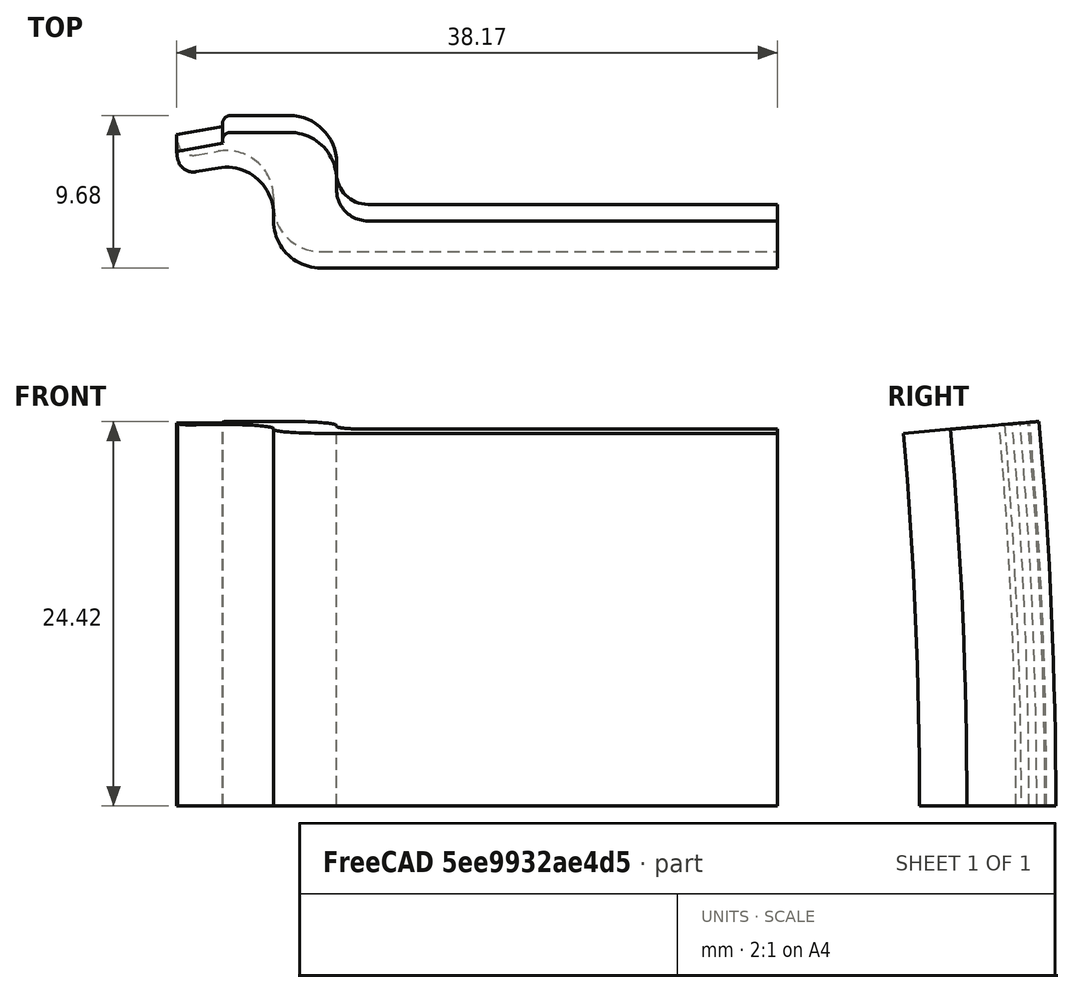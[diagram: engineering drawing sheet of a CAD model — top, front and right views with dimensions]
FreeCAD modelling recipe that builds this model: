
FCSTD DOCUMENT  (FreeCAD 0.16R)
Label: BeadLock5
License: All rights reserved
LicenseURL: http://en.wikipedia.org/wiki/All_rights_reserved
objects: PartDesign::Fillet×6, Sketcher::SketchObject×1, PartDesign::Revolution×1, Mesh::Feature×1
note: 9 computed .brp shape members not serialized (recipe doc carries the construction recipe); baked Part::Feature solids carry a one-line shape summary decoded from their .brp

FEATURE [Sketcher::SketchObject] Sketch
  sketch-geometry (10):
    g0: LineSegment StartX=0 StartY=279 StartZ=0 EndX=2.95442 EndY=279.521 EndZ=0
    g1: LineSegment StartX=2.95442 StartY=279.521 StartZ=0 EndX=2.83287 EndY=280.21 EndZ=0
    g2: LineSegment StartX=0.260472 StartY=277.523 StartZ=0 EndX=0 EndY=279 EndZ=0
    g3: LineSegment StartX=0.260472 StartY=277.523 StartZ=0 EndX=6.16932 EndY=278.565 EndZ=0
    g4: LineSegment StartX=6.16932 StartY=278.565 StartZ=0 EndX=6.16932 EndY=271.565 EndZ=0
    g5: LineSegment StartX=6.16932 StartY=271.565 StartZ=0 EndX=38.1693 EndY=271.565 EndZ=0
    g6: LineSegment StartX=38.1693 StartY=271.565 StartZ=0 EndX=38.1693 EndY=274.565 EndZ=0
    g7: LineSegment StartX=2.83287 StartY=280.21 StartZ=0 EndX=10.1693 EndY=280.21 EndZ=0
    g8: LineSegment StartX=10.1693 StartY=280.21 StartZ=0 EndX=10.1693 EndY=274.565 EndZ=0
    g9: LineSegment StartX=10.1693 StartY=274.565 StartZ=0 EndX=38.1693 EndY=274.565 EndZ=0
  constraints (30):
    c: PointOnObject(g0,g-2)
    c: DistanceY(g0) = 279
    c: Distance(g0) = 3
    c: Coincident(g1,g0)
    c: Distance(g1) = 0.7
    c: Coincident(g2,g0)
    c: Distance(g2) = 1.5
    c: Coincident(g3,g2)
    c: Distance(g3) = 6
    c: Vertical(g4)
    c: Coincident(g4,g3)
    c: Distance(g4) = 7
    c: Horizontal(g5)
    c: Coincident(g5,g4)
    c: Distance(g5) = 32
    c: Vertical(g6)
    c: Coincident(g5,g6)
    c: Distance(g6) = 3
    c: Parallel(g0,g3)
    c: Perpendicular(g0,g1)
    c: Angle(g3) = 0.174533
    c: Perpendicular(g2,g3)
    c: Coincident(g1,g7)
    c: Horizontal(g7)
    c: Coincident(g7,g8)
    c: Coincident(g8,g9)
    c: Coincident(g9,g6)
    c: Horizontal(g9)
    c: Parallel(g8,g4)
    c: Distance(g8,g4) = 4
FEATURE [PartDesign::Revolution] Revolution
  Angle = 5
  Axis = (1,0,0)
  Base = (0,0,0)
  ReferenceAxis = -> Sketch [H_Axis]
  Sketch = -> Sketch
FEATURE [PartDesign::Fillet] Fillet
  Base = -> Revolution [Edge23]
  Radius = 3
FEATURE [PartDesign::Fillet] Fillet001
  Base = -> Fillet [Edge3]
  Radius = 3
FEATURE [PartDesign::Fillet] Fillet002
  Base = -> Fillet001 [Edge35]
  Radius = 3
FEATURE [PartDesign::Fillet] Fillet003
  Base = -> Fillet002 [Edge15]
  Radius = 2
FEATURE [PartDesign::Fillet] Fillet004
  Base = -> Fillet003 [Edge36]
  Radius = 1
FEATURE [PartDesign::Fillet] Fillet005
  Base = -> Fillet004 [Edge25]
  Radius = 0.5
FEATURE [Mesh::Feature] Mesh  label="Fillet005 (Meshed)"
